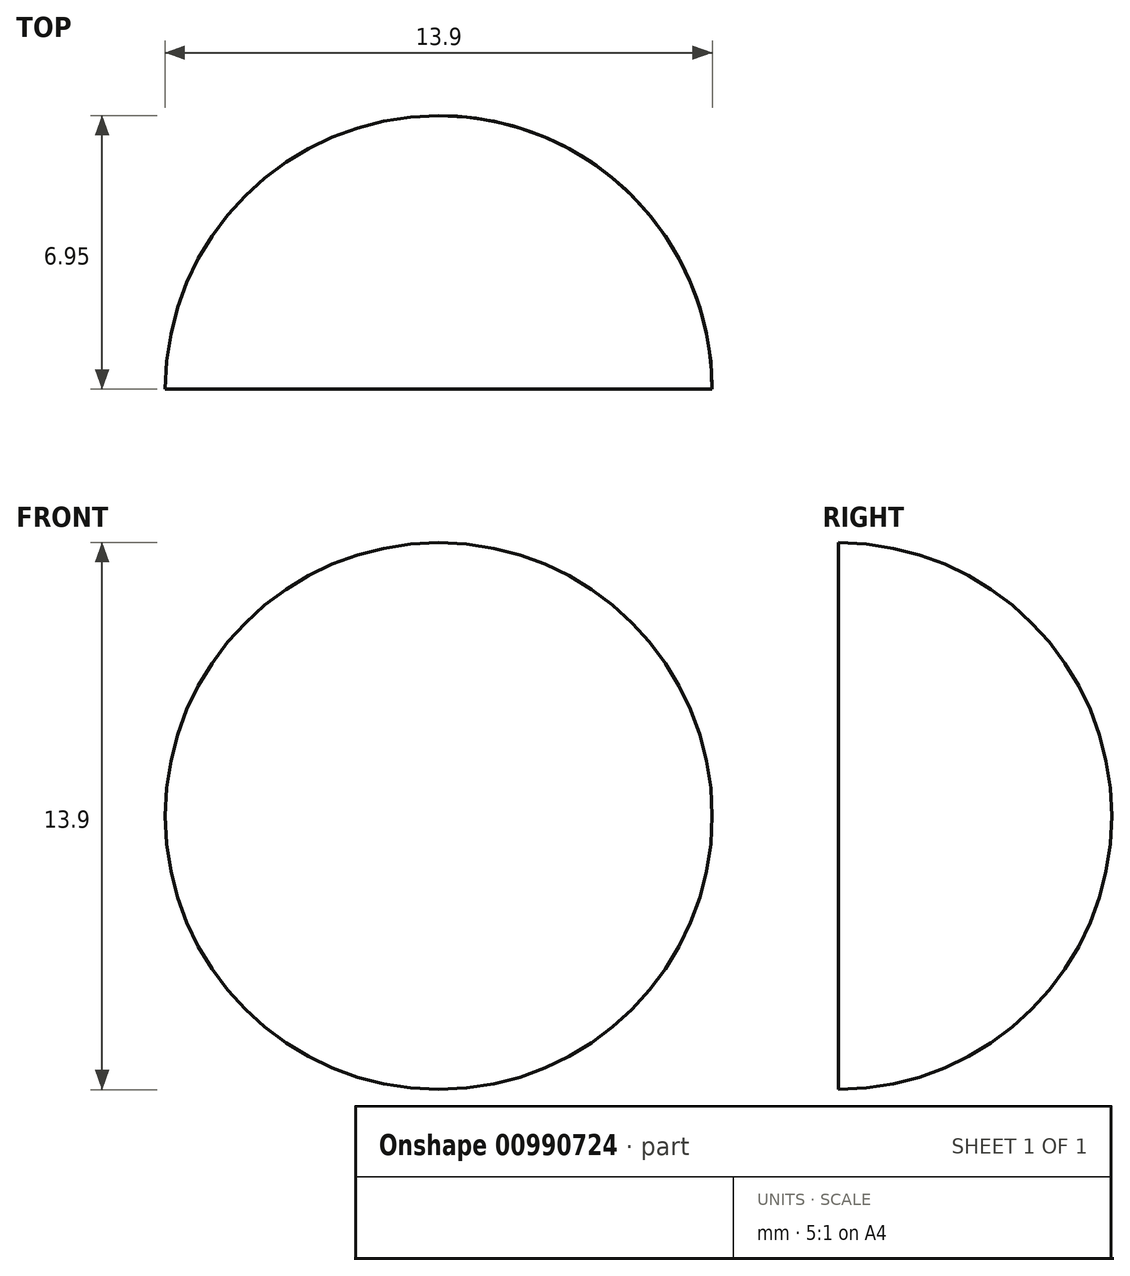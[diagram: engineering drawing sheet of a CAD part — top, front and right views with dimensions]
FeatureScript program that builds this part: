
annotation { "Feature Type Name" : "Feature", "Feature Type Description" : "" }
export const myFeature = defineFeature(function(context is Context, id is Id, definition is map)
    precondition{}
    {
        {
            var Q0;
            Q0=qCreatedBy(makeId("Top.planeOp"),FACE);
            var sketch = newSketch(context, id + "F0", { "sketchPlane" : qUnion([Q0])});
            skArc(sketch, "E0", {"start": v(0, 6.95) * mm, "mid": v(-4.91, 4.91) * mm, "end": v(-6.95, 0) * mm});
            skLineSegment(sketch, "E1", {"start": v(0, 6.95) * mm, "end": v(0, 0) * mm, "construction": true});
            skLineSegment(sketch, "E2", {"start": v(0, 6.95) * mm, "end": v(0, 0) * mm});
            skLineSegment(sketch, "E3", {"start": v(0, 0) * mm, "end": v(-6.95, 0) * mm});
            skSolve(sketch);
        }
        {
            var Q0;
            Q0=makeQuery(id+"F0.imprint","IMPRINT",FACE,{"disambiguationData":[TD([[makeQuery(id+"F0.imprint","IMPRINT",EDGE,{"derivedFrom":sQuery(id+"F0.wireOp",EDGE,"E0")}),1.0]])]});
            var Q1;
            Q1=sQuery(id+"F0.wireOp",EDGE,"E2");
            revolve(context, id + "F1", {"surfaceOperationType" : NewSurfaceOperationType.NEW, "entities" : qUnion([Q0]), "axis" : qUnion([Q1]), "revolveType" : RevolveType.FULL});
        }
    });
